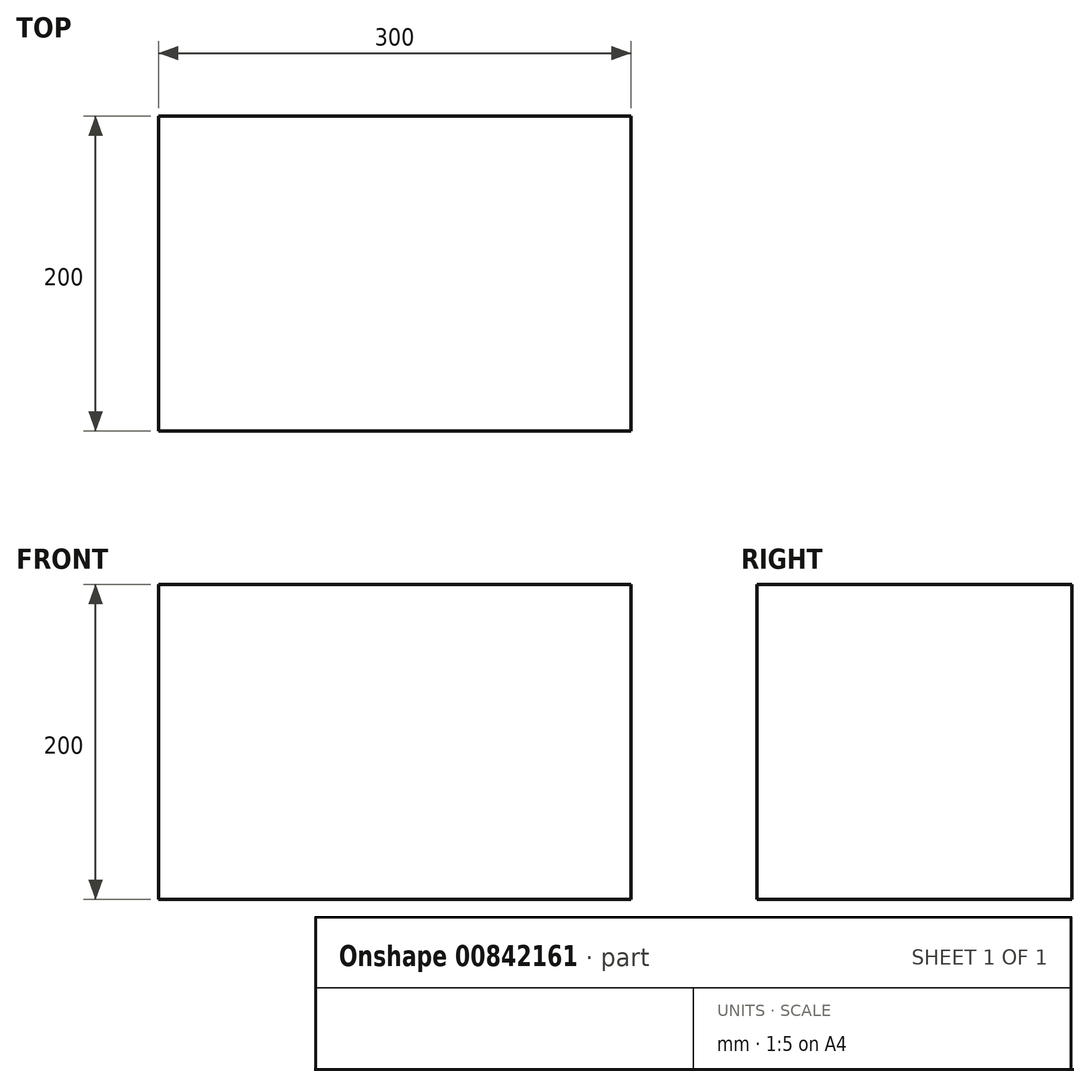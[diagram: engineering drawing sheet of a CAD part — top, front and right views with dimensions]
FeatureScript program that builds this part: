
annotation { "Feature Type Name" : "Feature", "Feature Type Description" : "" }
export const myFeature = defineFeature(function(context is Context, id is Id, definition is map)
    precondition{}
    {
        {
            var Q0;
            Q0=qCreatedBy(makeId("Top.planeOp"),FACE);
            var sketch = newSketch(context, id + "F0", { "sketchPlane" : qUnion([Q0])});
            skLineSegment(sketch, "E0.bottom", {"start": v(150, 100) * mm, "end": v(-150, 100) * mm});
            skLineSegment(sketch, "E0.top", {"start": v(150, -100) * mm, "end": v(-150, -100) * mm});
            skLineSegment(sketch, "E0.left", {"start": v(150, 100) * mm, "end": v(150, -100) * mm});
            skLineSegment(sketch, "E0.right", {"start": v(-150, 100) * mm, "end": v(-150, -100) * mm});
            skPoint(sketch, "E0.middle", {"position": v(0, 0) * mm});
            skSolve(sketch);
        }
        {
            var Q0;
            Q0=makeQuery(id+"F0.imprint","IMPRINT",FACE,{"disambiguationData":[TD([[makeQuery(id+"F0.imprint","IMPRINT",EDGE,{"derivedFrom":sQuery(id+"F0.wireOp",EDGE,"E0.bottom")}),1.0]])]});
            extrude(context, id + "F1", {"entities" : qUnion([Q0]), "depth" : 200 * mm, "offsetDistance" : 25 * mm});
        }
    });
